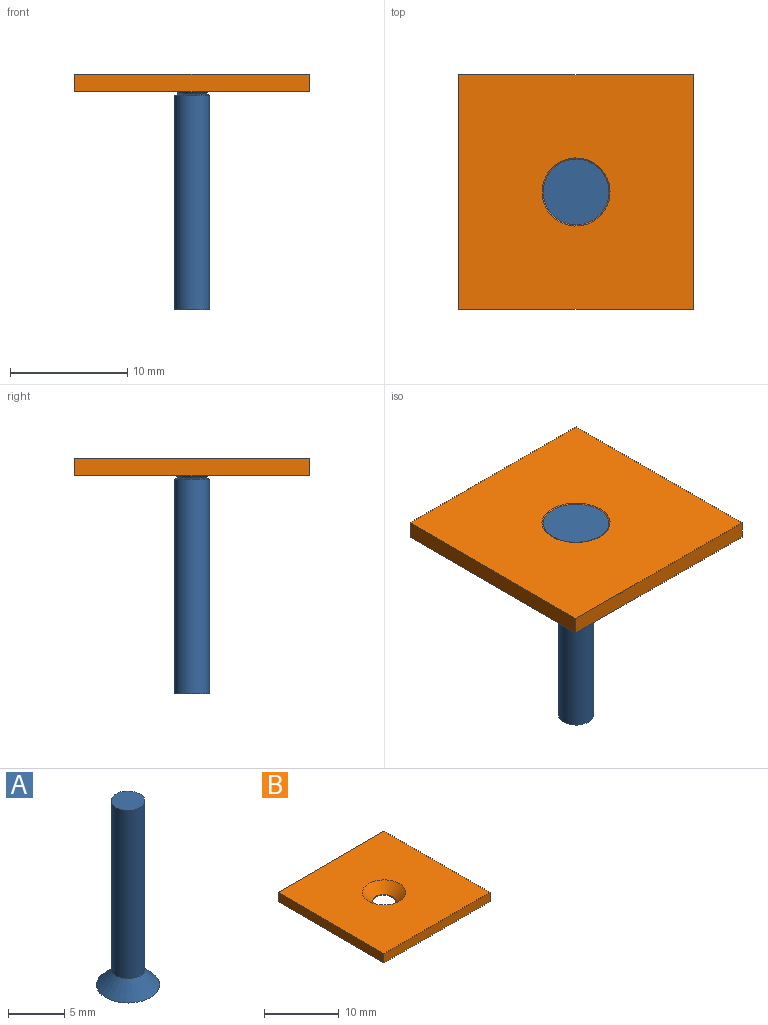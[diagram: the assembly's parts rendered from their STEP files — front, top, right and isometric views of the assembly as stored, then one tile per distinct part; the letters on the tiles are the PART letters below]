
ASSEMBLY  parts=2 mates=1
PART A: 6 faces, bbox 5.6x5.6x20 mm
  f0: plane 3x3mm, normal (0,0,1), area 7.1mm2, adj f1
  f1: cylinder r=1.5mm len=18.28mm, axis (0,0,1), area 172.2mm2, adj f0,f2
  f2: cone r=1.5mm half-angle=78deg, axis (0,0,1), area 2.6mm2, adj f1,f3
  f3: torus R=1.24mm, axis (0,0,1), area 0.5mm2, adj f2,f4
  f4: cone r=1.2mm half-angle=45deg, axis (0,0,-1), area 28.4mm2, adj f3,f5
  f5: plane 5.6x5.6mm, normal (0,0,-1), area 24.6mm2, adj f4
PART B: 8 faces, bbox 20x20x1.5 mm
  f0: plane 20x1.5mm, normal (0,-1,0), area 30mm2, adj f1,f4,f5,f6
  f1: plane 20x1.5mm, normal (1,0,0), area 30mm2, adj f0,f2,f5,f6
  f2: plane 20x1.5mm, normal (0,1,0), area 30mm2, adj f1,f4,f5,f6
  f3: cylinder r=1.5mm len=3mm, axis (0,0,-1), area 0.9mm2, adj f6,f7
  f4: plane 20x1.5mm, normal (-1,0,0), area 30mm2, adj f0,f2,f5,f6
  f5: plane 20x20mm, normal (0,0,1), area 373.6mm2, adj f0,f1,f2,f4,f7
  f6: plane 20x20mm, normal (0,0,-1), area 392.9mm2, adj f0,f1,f2,f3,f4
  f7: cone r=1.5mm half-angle=45deg, axis (0,0,1), area 27.4mm2, adj f3,f5
PLACE A rot(axis=(1,0,0),180deg) t=(-3.88,9.47,-5.75)mm
PLACE B t=(6.12,-20.53,-7.7)mm
MATE cylindrical A.f1 <-> B.f3  axis (0,0,-1) through (-3.88,9.47,-5.75)mm
